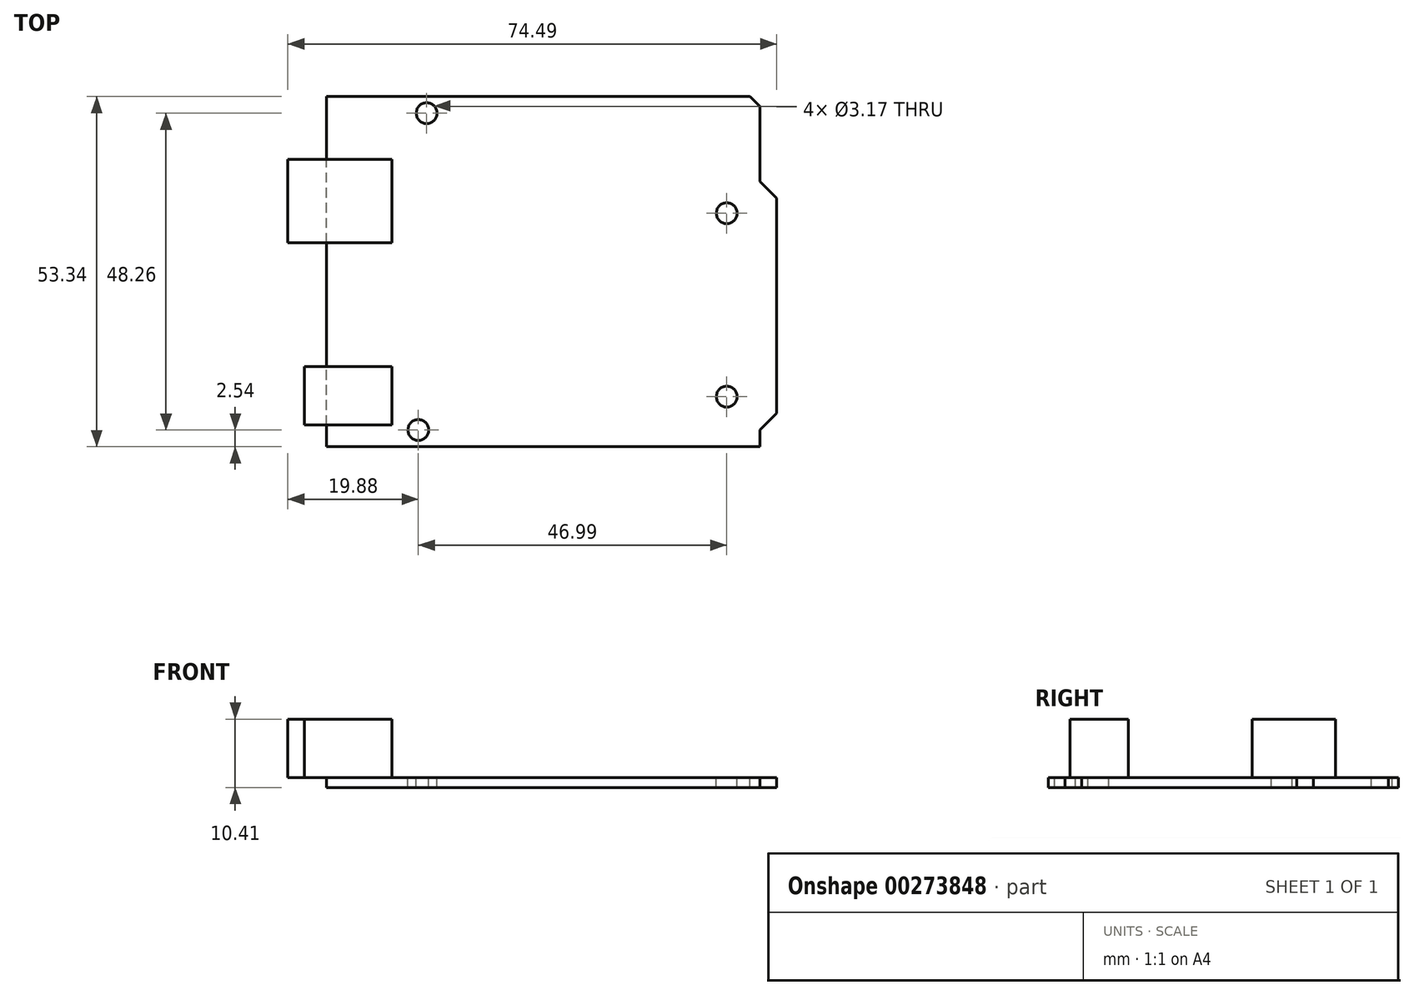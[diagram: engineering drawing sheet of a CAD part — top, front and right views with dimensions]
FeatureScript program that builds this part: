
annotation { "Feature Type Name" : "Feature", "Feature Type Description" : "" }
export const myFeature = defineFeature(function(context is Context, id is Id, definition is map)
    precondition{}
    {
        {
            var Q0;
            Q0=qCreatedBy(makeId("Top.planeOp"),FACE);
            var sketch = newSketch(context, id + "F0", { "sketchPlane" : qUnion([Q0])});
            skLineSegment(sketch, "E0.bottom", {"start": v(0, 0) * mm, "end": v(68.58, 0) * mm});
            skLineSegment(sketch, "E0.top", {"start": v(0, 53.34) * mm, "end": v(68.58, 53.34) * mm});
            skLineSegment(sketch, "E0.left", {"start": v(0, 0) * mm, "end": v(0, 53.34) * mm});
            skLineSegment(sketch, "E0.right", {"start": v(68.58, 0) * mm, "end": v(68.58, 53.34) * mm});
            skLineSegment(sketch, "E1", {"start": v(66.04, 0) * mm, "end": v(66.04, 2.54) * mm});
            skLineSegment(sketch, "E2", {"start": v(66.04, 2.54) * mm, "end": v(68.58, 5.08) * mm});
            skLineSegment(sketch, "E3", {"start": v(64.52, 53.34) * mm, "end": v(66.04, 51.82) * mm});
            skLineSegment(sketch, "E4", {"start": v(66.04, 51.82) * mm, "end": v(66.04, 40.39) * mm});
            skLineSegment(sketch, "E5", {"start": v(66.04, 40.39) * mm, "end": v(68.58, 37.85) * mm});
            skCircle(sketch, "E6", {"center": v(15.24, 50.8) * mm, "radius": 1.59 * mm});
            skCircle(sketch, "E7", {"center": v(13.97, 2.54) * mm, "radius": 1.59 * mm});
            skCircle(sketch, "E8", {"center": v(60.96, 7.62) * mm, "radius": 1.59 * mm});
            skCircle(sketch, "E9", {"center": v(60.96, 35.56) * mm, "radius": 1.59 * mm});
            skSolve(sketch);
        }
        {
            var Q0;
            {var subQ5=sQuery(id+"F0.wireOp",EDGE,"QQRKJGLR-GZdt-b5F1-wHk7-w8ApHPgQRY9v.right");Q0=makeQuery(id+"F0.imprint","IMPRINT",FACE,{"disambiguationData":[TD([[makeQuery(id+"F0.imprint","IMPRINT",EDGE,{"derivedFrom":subQ5}),-1.0]])]});}
            var Q1;
            {var subQ3=sQuery(id+"F0.wireOp",EDGE,"E1");Q1=makeQuery(id+"F0.imprint","IMPRINT",FACE,{"disambiguationData":[TD([[makeQuery(id+"F0.imprint","IMPRINT",EDGE,{"derivedFrom":subQ3}),1.0]])]});}
            extrude(context, id + "F1", {"entities" : qUnion([Q0, Q1]), "oppositeDirection" : true, "depth" : 1.52 * mm});
        }
        {
            var Q0;
            Q0=makeQuery(id+"F1.opExtrude","CAP_FACE",FACE,{"disambiguationData":[OSD([sQuery(id+"F0.wireOp",EDGE,"E0.bottom"),sQuery(id+"F0.wireOp",EDGE,"E0.top"),sQuery(id+"F0.wireOp",EDGE,"E0.left"),sQuery(id+"F0.wireOp",EDGE,"E0.right"),sQuery(id+"F0.wireOp",EDGE,"E1"),sQuery(id+"F0.wireOp",EDGE,"E2"),sQuery(id+"F0.wireOp",EDGE,"E3"),sQuery(id+"F0.wireOp",EDGE,"E4"),sQuery(id+"F0.wireOp",EDGE,"E5"),sQuery(id+"F0.wireOp",EDGE,"E6"),sQuery(id+"F0.wireOp",EDGE,"E7"),sQuery(id+"F0.wireOp",EDGE,"E8"),sQuery(id+"F0.wireOp",EDGE,"E9")])],"isStart":true});
            var sketch = newSketch(context, id + "F2", { "sketchPlane" : qUnion([Q0])});
            skLineSegment(sketch, "E10.bottom", {"start": v(-5.91, 43.74) * mm, "end": v(9.96, 43.74) * mm});
            skLineSegment(sketch, "E10.top", {"start": v(-5.91, 31.04) * mm, "end": v(9.96, 31.04) * mm});
            skLineSegment(sketch, "E10.left", {"start": v(-5.91, 43.74) * mm, "end": v(-5.91, 31.04) * mm});
            skLineSegment(sketch, "E10.right", {"start": v(9.96, 43.74) * mm, "end": v(9.96, 31.04) * mm});
            skLineSegment(sketch, "E11.bottom", {"start": v(9.96, 3.3) * mm, "end": v(-3.37, 3.3) * mm});
            skLineSegment(sketch, "E11.top", {"start": v(9.96, 12.2) * mm, "end": v(-3.37, 12.2) * mm});
            skLineSegment(sketch, "E11.left", {"start": v(9.96, 3.3) * mm, "end": v(9.96, 12.2) * mm});
            skLineSegment(sketch, "E11.right", {"start": v(-3.37, 3.3) * mm, "end": v(-3.37, 12.2) * mm});
            skSolve(sketch);
        }
        {
            var Q0;
            {var subQ0=sQuery(id+"F2.wireOp",EDGE,"E10.left");Q0=makeQuery(id+"F2.imprint","IMPRINT",FACE,{"disambiguationData":[TD([[makeQuery(id+"F2.imprint","IMPRINT",EDGE,{"derivedFrom":subQ0}),1.0]])]});}
            var Q1;
            {var subQ0=sQuery(id+"F2.wireOp",EDGE,"E10.right");Q1=makeQuery(id+"F2.imprint","IMPRINT",FACE,{"disambiguationData":[TD([[makeQuery(id+"F2.imprint","IMPRINT",EDGE,{"derivedFrom":subQ0}),-1.0]])]});}
            var Q2;
            {var subQ0=sQuery(id+"F2.wireOp",EDGE,"E11.right");Q2=makeQuery(id+"F2.imprint","IMPRINT",FACE,{"disambiguationData":[TD([[makeQuery(id+"F2.imprint","IMPRINT",EDGE,{"derivedFrom":subQ0}),-1.0]])]});}
            var Q3;
            {var subQ0=sQuery(id+"F2.wireOp",EDGE,"E11.left");Q3=makeQuery(id+"F2.imprint","IMPRINT",FACE,{"disambiguationData":[TD([[makeQuery(id+"F2.imprint","IMPRINT",EDGE,{"derivedFrom":subQ0}),1.0]])]});}
            extrude(context, id + "F3", {"entities" : qUnion([Q0, Q1, Q2, Q3]), "operationType" : NewBodyOperationType.ADD, "depth" : 8.9 * mm});
        }
    });
